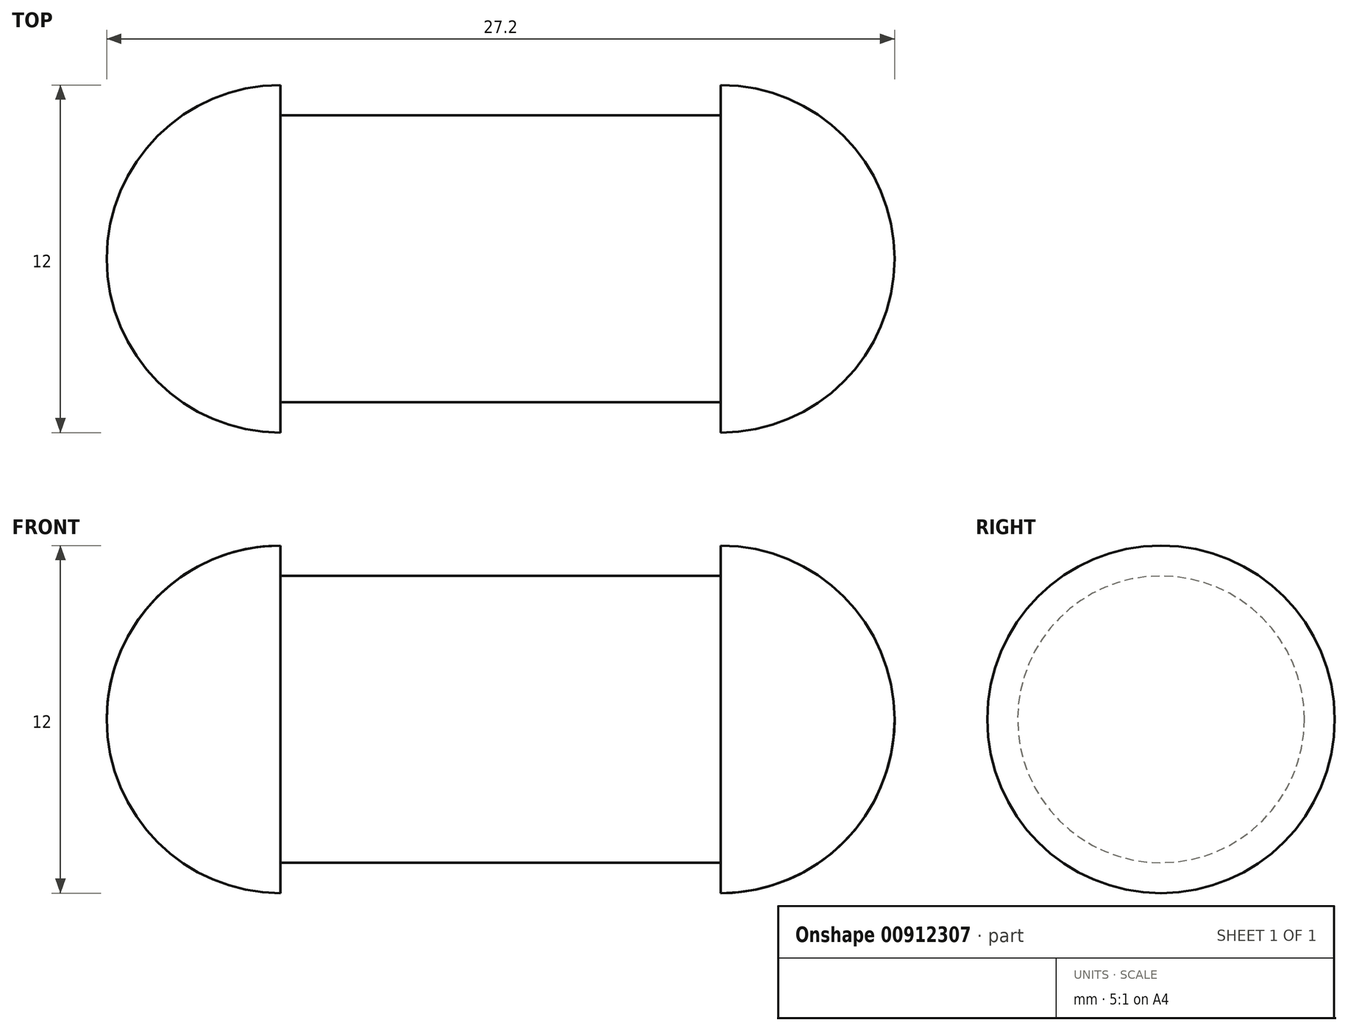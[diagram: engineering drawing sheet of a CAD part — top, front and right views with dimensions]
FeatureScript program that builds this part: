
annotation { "Feature Type Name" : "Feature", "Feature Type Description" : "" }
export const myFeature = defineFeature(function(context is Context, id is Id, definition is map)
    precondition{}
    {
        {
            var Q0;
            Q0=qCreatedBy(makeId("Front.planeOp"),FACE);
            var sketch = newSketch(context, id + "F0", { "sketchPlane" : qUnion([Q0])});
            skLineSegment(sketch, "E0.bottom", {"start": v(0, 0) * mm, "end": v(-15.2, 0) * mm});
            skLineSegment(sketch, "E0.top", {"start": v(0, 9.9) * mm, "end": v(-15.2, 9.9) * mm});
            skLineSegment(sketch, "E0.left", {"start": v(0, 0) * mm, "end": v(0, 9.9) * mm});
            skLineSegment(sketch, "E0.right", {"start": v(-15.2, 0) * mm, "end": v(-15.2, 9.9) * mm});
            skLineSegment(sketch, "E1", {"start": v(-15.2, 9.9) * mm, "end": v(-15.2, 10.95) * mm});
            skLineSegment(sketch, "E2", {"start": v(-15.2, 0) * mm, "end": v(-15.2, -1.05) * mm});
            skLineSegment(sketch, "E3", {"start": v(0, 9.9) * mm, "end": v(0, 10.95) * mm});
            skLineSegment(sketch, "E4", {"start": v(0, 0) * mm, "end": v(0, -1.05) * mm});
            skArc(sketch, "E5", {"start": v(-15.2, 10.95) * mm, "mid": v(-21.2, 4.95) * mm, "end": v(-15.2, -1.05) * mm});
            skArc(sketch, "E6", {"start": v(0, -1.05) * mm, "mid": v(6, 4.95) * mm, "end": v(0, 10.95) * mm});
            skLineSegment(sketch, "E7", {"start": v(-21.2, 4.95) * mm, "end": v(6, 4.95) * mm});
            skSolve(sketch);
        }
        {
            var Q0;
            {var subQ0=sQuery(id+"F0.wireOp",EDGE,"E4");Q0=makeQuery(id+"F0.imprint","IMPRINT",FACE,{"disambiguationData":[TD([[makeQuery(id+"F0.imprint","IMPRINT",EDGE,{"derivedFrom":subQ0}),1.0]])]});}
            var Q1;
            {var subQ0=sQuery(id+"F0.wireOp",EDGE,"E2");Q1=makeQuery(id+"F0.imprint","IMPRINT",FACE,{"disambiguationData":[TD([[makeQuery(id+"F0.imprint","IMPRINT",EDGE,{"derivedFrom":subQ0}),-1.0]])]});}
            var Q2;
            {var subQ0=sQuery(id+"F0.wireOp",EDGE,"E0.bottom");Q2=makeQuery(id+"F0.imprint","IMPRINT",FACE,{"disambiguationData":[TD([[makeQuery(id+"F0.imprint","IMPRINT",EDGE,{"derivedFrom":subQ0}),-1.0]])]});}
            var Q3;
            Q3=sQuery(id+"F0.wireOp",EDGE,"E7");
            revolve(context, id + "F1", {"surfaceOperationType" : NewSurfaceOperationType.NEW, "entities" : qUnion([Q0, Q1, Q2]), "axis" : qUnion([Q3]), "revolveType" : RevolveType.FULL});
        }
    });
